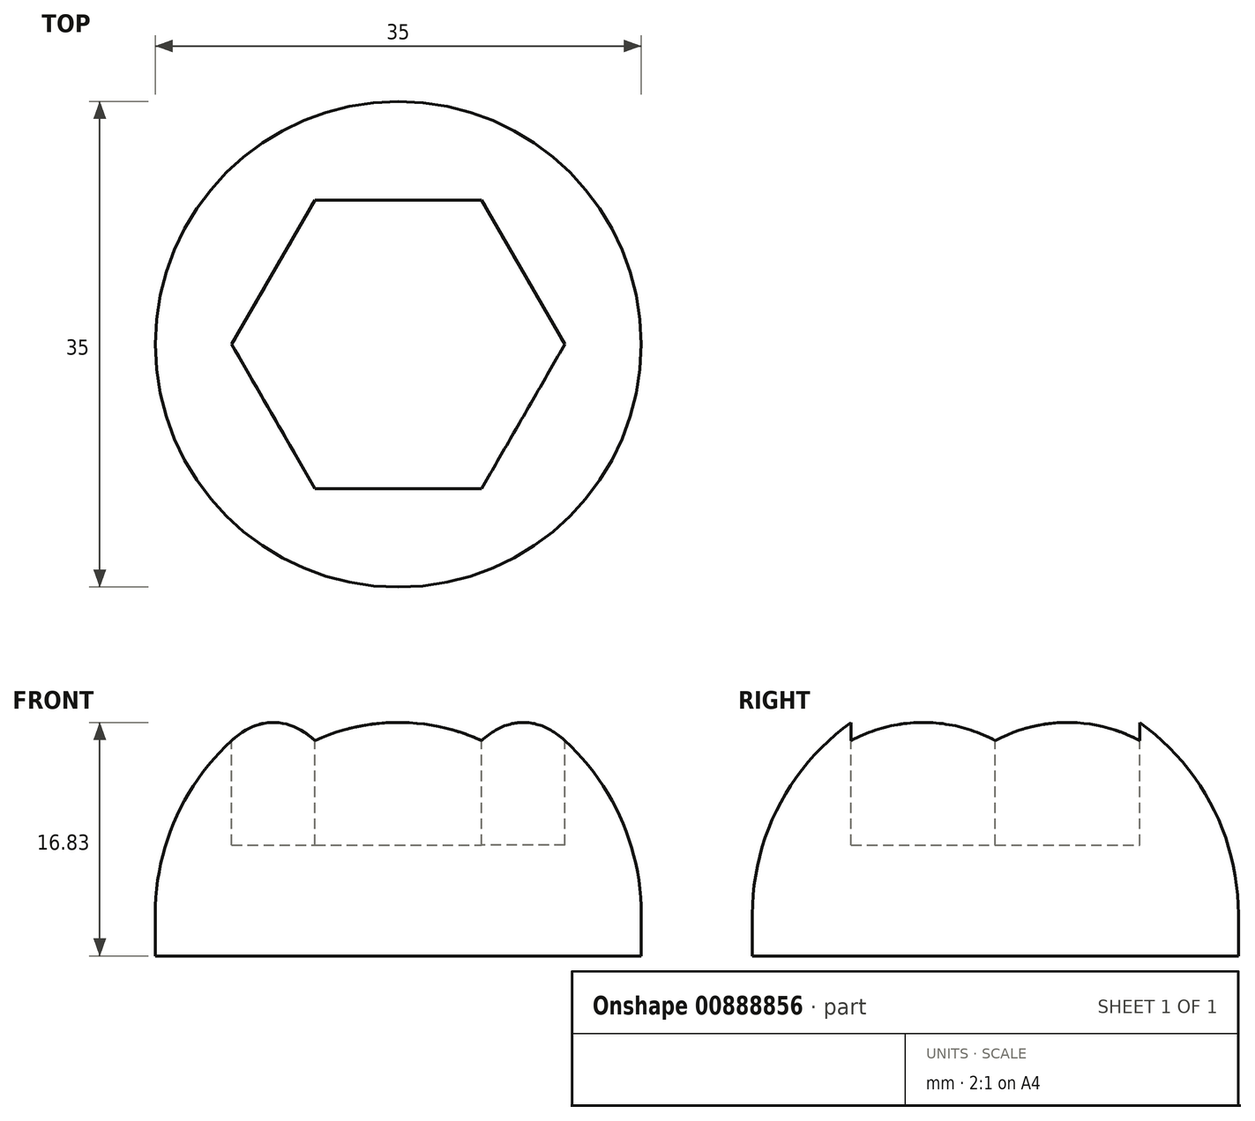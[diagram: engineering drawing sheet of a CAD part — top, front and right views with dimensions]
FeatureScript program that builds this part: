
annotation { "Feature Type Name" : "Feature", "Feature Type Description" : "" }
export const myFeature = defineFeature(function(context is Context, id is Id, definition is map)
    precondition{}
    {
        {
            var Q0;
            Q0=qCreatedBy(makeId("Top.planeOp"),FACE);
            var sketch = newSketch(context, id + "F0", { "sketchPlane" : qUnion([Q0])});
            skCircle(sketch, "E0", {"center": v(0, 0) * mm, "radius": 17.5 * mm});
            skSolve(sketch);
        }
        {
            var Q0;
            Q0=makeQuery(id+"F0.imprint","IMPRINT",FACE,{"disambiguationData":[TD([[makeQuery(id+"F0.imprint","IMPRINT",EDGE,{"derivedFrom":sQuery(id+"F0.wireOp",EDGE,"E0")}),1.0]])]});
            extrude(context, id + "F1", {"entities" : qUnion([Q0]), "depth" : 20 * mm, "offsetDistance" : 25 * mm});
        }
        {
            var Q0;
            Q0=makeQuery(id+"F1.opExtrude","CAP_FACE",FACE,{"disambiguationData":[OSD([sQuery(id+"F0.wireOp",EDGE,"E0")])],"isStart":false});
            var sketch = newSketch(context, id + "F2", { "sketchPlane" : qUnion([Q0])});
            skCircle(sketch, "E1.cCircle", {"center": v(0, 0) * mm, "radius": 10.4 * mm, "construction": true});
            skLineSegment(sketch, "E1.0", {"start": v(-6, 10.4) * mm, "end": v(6, 10.4) * mm});
            skLineSegment(sketch, "E1.1", {"start": v(6, 10.4) * mm, "end": v(12, 0) * mm});
            skLineSegment(sketch, "E1.2", {"start": v(12, 0) * mm, "end": v(6, -10.4) * mm});
            skLineSegment(sketch, "E1.3", {"start": v(6, -10.4) * mm, "end": v(-6, -10.4) * mm});
            skLineSegment(sketch, "E1.4", {"start": v(-6, -10.4) * mm, "end": v(-12, 0) * mm});
            skLineSegment(sketch, "E1.5", {"start": v(-12, 0) * mm, "end": v(-6, 10.4) * mm});
            skPoint(sketch, "E1.0.midPoint", {"position": v(0, 10.4) * mm});
            skSolve(sketch);
        }
        {
            var Q0;
            Q0=makeQuery(id+"F2.imprint","IMPRINT",FACE,{"disambiguationData":[TD([[makeQuery(id+"F2.imprint","IMPRINT",EDGE,{"derivedFrom":sQuery(id+"F2.wireOp",EDGE,"E1.0")}),-1.0]])]});
            extrude(context, id + "F3", {"entities" : qUnion([Q0]), "operationType" : NewBodyOperationType.REMOVE, "oppositeDirection" : true, "depth" : 12 * mm, "offsetDistance" : 25 * mm});
        }
        {
            var Q0;
            Q0=makeQuery(id+"F1.opExtrude","CAP_EDGE",EDGE,{"disambiguationData":[OSD([sQuery(id+"F0.wireOp",EDGE,"E0")])],"isStart":false});
            fillet(context, id + "F4", {"entities" : qUnion([Q0]), "radius" : 17 * mm, "tangentPropagation" : true, "allowEdgeOverflow" : false});
        }
    });
